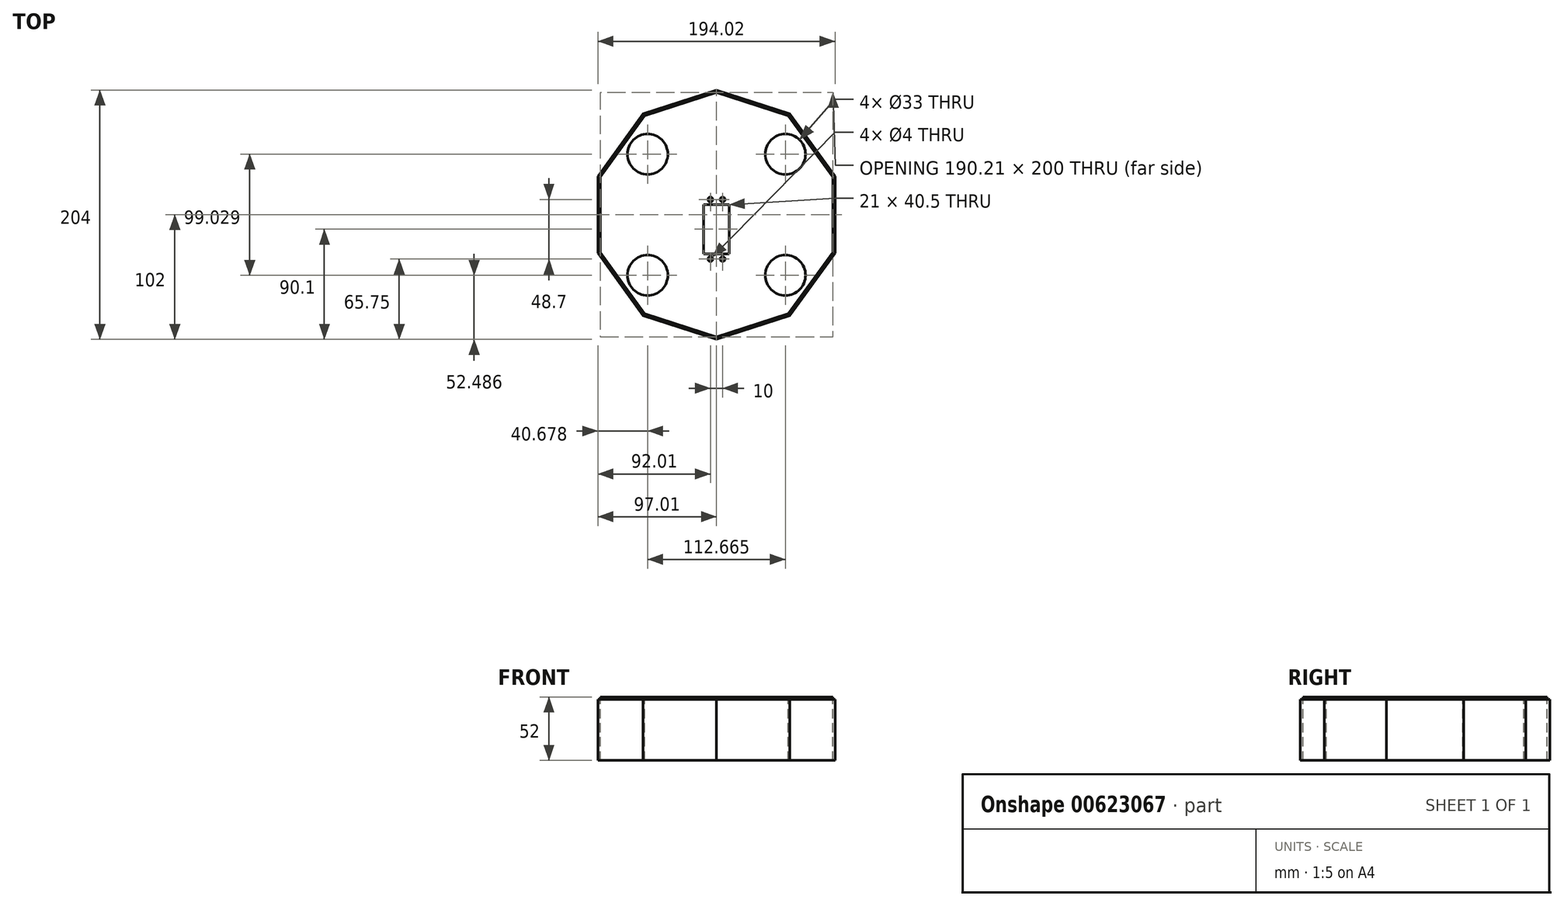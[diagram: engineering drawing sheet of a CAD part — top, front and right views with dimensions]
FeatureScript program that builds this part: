
annotation { "Feature Type Name" : "Feature", "Feature Type Description" : "" }
export const myFeature = defineFeature(function(context is Context, id is Id, definition is map)
    precondition{}
    {
        {
            var Q0;
            Q0=qCreatedBy(makeId("Top.planeOp"),FACE);
            var sketch = newSketch(context, id + "F0", { "sketchPlane" : qUnion([Q0])});
            skCircle(sketch, "E0.cCircle", {"center": v(0, 0) * mm, "radius": 100 * mm, "construction": true});
            skLineSegment(sketch, "E0.0", {"start": v(0, 100) * mm, "end": v(58.78, 80.9) * mm});
            skLineSegment(sketch, "E0.1", {"start": v(58.78, 80.9) * mm, "end": v(95.1, 30.9) * mm});
            skLineSegment(sketch, "E0.2", {"start": v(95.1, 30.9) * mm, "end": v(95.1, -30.9) * mm});
            skLineSegment(sketch, "E0.3", {"start": v(95.1, -30.9) * mm, "end": v(58.78, -80.9) * mm});
            skLineSegment(sketch, "E0.4", {"start": v(58.78, -80.9) * mm, "end": v(0, -100) * mm});
            skLineSegment(sketch, "E0.5", {"start": v(0, -100) * mm, "end": v(-58.78, -80.9) * mm});
            skLineSegment(sketch, "E0.6", {"start": v(-58.78, -80.9) * mm, "end": v(-95.1, -30.9) * mm});
            skLineSegment(sketch, "E0.7", {"start": v(-95.1, -30.9) * mm, "end": v(-95.1, 30.9) * mm});
            skLineSegment(sketch, "E0.8", {"start": v(-95.1, 30.9) * mm, "end": v(-58.78, 80.9) * mm});
            skLineSegment(sketch, "E0.9", {"start": v(-58.78, 80.9) * mm, "end": v(0, 100) * mm});
            skLineSegment(sketch, "E1.bottom", {"start": v(-10.5, 8.35) * mm, "end": v(10.5, 8.35) * mm});
            skLineSegment(sketch, "E1.top", {"start": v(-10.5, -32.15) * mm, "end": v(10.5, -32.15) * mm});
            skLineSegment(sketch, "E1.left", {"start": v(-10.5, 8.35) * mm, "end": v(-10.5, -32.15) * mm});
            skLineSegment(sketch, "E1.right", {"start": v(10.5, 8.35) * mm, "end": v(10.5, -32.15) * mm});
            skCircle(sketch, "E2", {"center": v(-5, 12.45) * mm, "radius": 2 * mm});
            skCircle(sketch, "E3", {"center": v(5, 12.45) * mm, "radius": 2 * mm});
            skCircle(sketch, "E4", {"center": v(-5, -36.25) * mm, "radius": 2 * mm});
            skCircle(sketch, "E5", {"center": v(5, -36.25) * mm, "radius": 2 * mm});
            skCircle(sketch, "E6", {"center": v(-56.33, 49.51) * mm, "radius": 16.5 * mm});
            skCircle(sketch, "E7", {"center": v(56.33, 49.51) * mm, "radius": 16.5 * mm});
            skCircle(sketch, "E8", {"center": v(-56.33, -49.51) * mm, "radius": 16.5 * mm});
            skCircle(sketch, "E9", {"center": v(56.33, -49.51) * mm, "radius": 16.5 * mm});
            skCircle(sketch, "E10.cCircle", {"center": v(0, 0) * mm, "radius": 102 * mm, "construction": true});
            skLineSegment(sketch, "E10.0", {"start": v(0, 102) * mm, "end": v(59.95, 82.52) * mm});
            skLineSegment(sketch, "E10.1", {"start": v(59.95, 82.52) * mm, "end": v(97, 31.52) * mm});
            skLineSegment(sketch, "E10.2", {"start": v(97, 31.52) * mm, "end": v(97, -31.52) * mm});
            skLineSegment(sketch, "E10.3", {"start": v(97, -31.52) * mm, "end": v(59.95, -82.52) * mm});
            skLineSegment(sketch, "E10.4", {"start": v(59.95, -82.52) * mm, "end": v(0, -102) * mm});
            skLineSegment(sketch, "E10.5", {"start": v(0, -102) * mm, "end": v(-59.95, -82.52) * mm});
            skLineSegment(sketch, "E10.6", {"start": v(-59.95, -82.52) * mm, "end": v(-97, -31.52) * mm});
            skLineSegment(sketch, "E10.7", {"start": v(-97, -31.52) * mm, "end": v(-97, 31.52) * mm});
            skLineSegment(sketch, "E10.8", {"start": v(-97, 31.52) * mm, "end": v(-59.95, 82.52) * mm});
            skLineSegment(sketch, "E10.9", {"start": v(-59.95, 82.52) * mm, "end": v(0, 102) * mm});
            skSolve(sketch);
        }
        {
            var Q0;
            Q0=makeQuery(id+"F0.imprint","IMPRINT",FACE,{"disambiguationData":[TD([[makeQuery(id+"F0.imprint","IMPRINT",EDGE,{"derivedFrom":sQuery(id+"F0.wireOp",EDGE,"E0.0")}),-1.0]])]});
            extrude(context, id + "F1", {"entities" : qUnion([Q0]), "depth" : 2 * mm, "offsetDistance" : 25 * mm});
        }
        {
            var Q0;
            Q0 = qSketchRegion(id + "F0", true);
            extrude(context, id + "F2", {"entities" : qUnion([Q0]), "depth" : -50 * mm, "offsetDistance" : 25 * mm});
        }
    });
